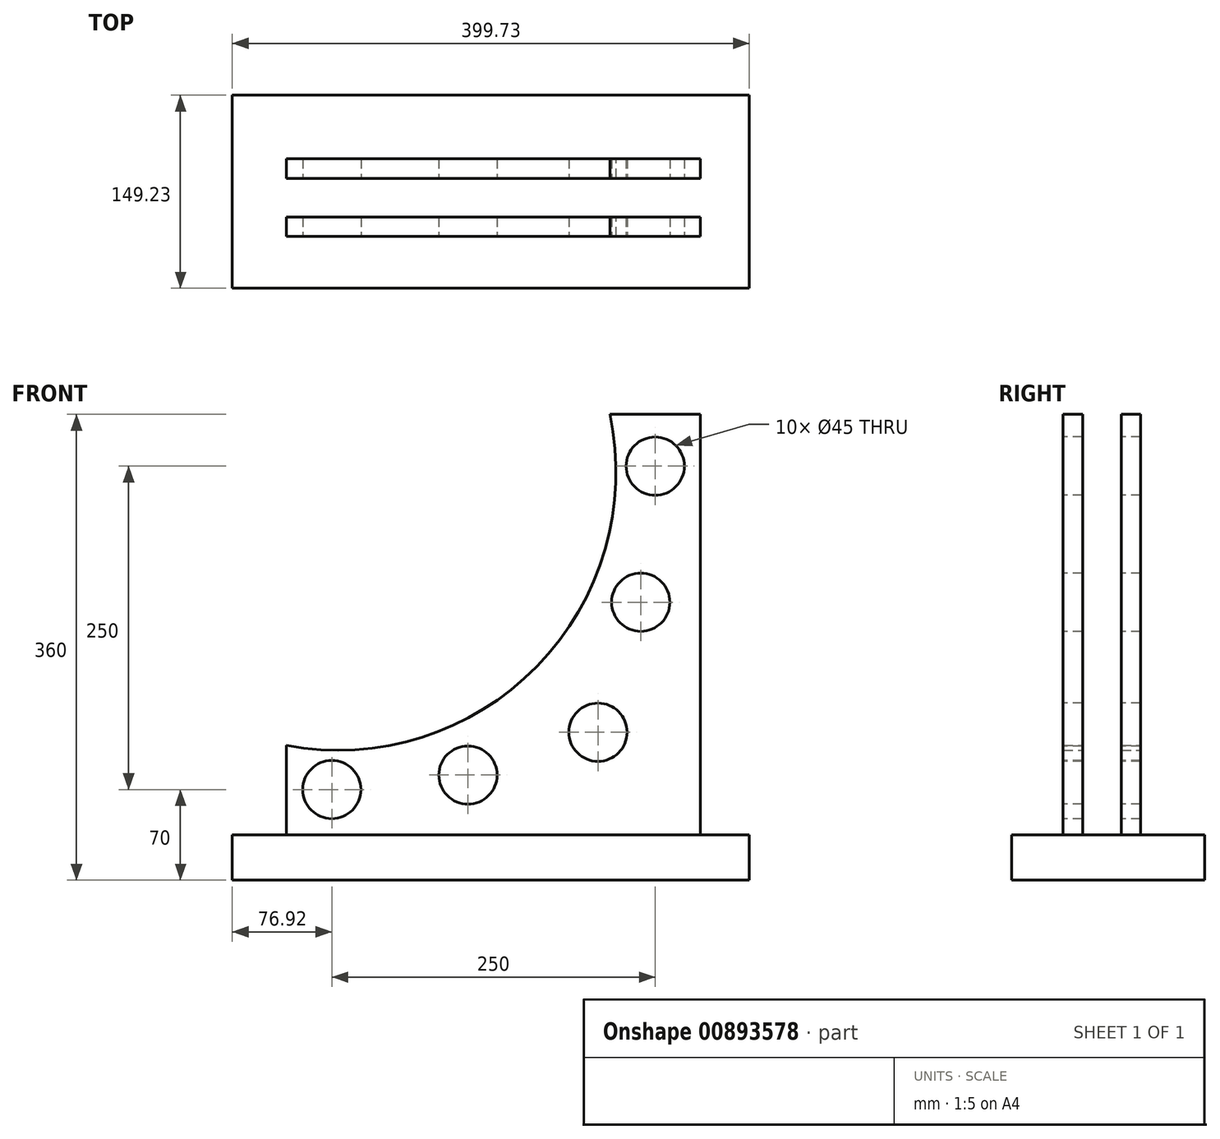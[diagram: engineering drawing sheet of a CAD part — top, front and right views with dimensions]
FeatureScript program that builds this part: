
annotation { "Feature Type Name" : "Feature", "Feature Type Description" : "" }
export const myFeature = defineFeature(function(context is Context, id is Id, definition is map)
    precondition{}
    {
        {
            var Q0;
            Q0=qCreatedBy(makeId("Top.planeOp"),FACE);
            var sketch = newSketch(context, id + "F0", { "sketchPlane" : qUnion([Q0])});
            skLineSegment(sketch, "E0.bottom", {"start": v(-320, -101.07) * mm, "end": v(0, -101.07) * mm});
            skLineSegment(sketch, "E0.top", {"start": v(-320, -41.07) * mm, "end": v(0, -41.07) * mm});
            skLineSegment(sketch, "E0.left", {"start": v(-320, -101.07) * mm, "end": v(-320, -41.07) * mm});
            skLineSegment(sketch, "E0.right", {"start": v(0, -101.07) * mm, "end": v(0, -41.07) * mm});
            skSolve(sketch);
        }
        {
            var Q0;
            Q0=makeQuery(id+"F0.imprint","IMPRINT",FACE,{"disambiguationData":[TD([[makeQuery(id+"F0.imprint","IMPRINT",EDGE,{"derivedFrom":sQuery(id+"F0.wireOp",EDGE,"E0.bottom")}),1.0]])]});
            extrude(context, id + "F1", {"entities" : qUnion([Q0]), "depth" : 360 * mm, "offsetDistance" : 25 * mm});
        }
        {
            var Q0;
            Q0=makeQuery(id+"F1.opExtrude","SWEPT_FACE",FACE,{"disambiguationData":[OSD([sQuery(id+"F0.wireOp",EDGE,"E0.bottom")])]});
            var sketch = newSketch(context, id + "F2", { "sketchPlane" : qUnion([Q0])});
            skCircle(sketch, "E1", {"center": v(-35, 320) * mm, "radius": 22.5 * mm});
            skCircle(sketch, "E2", {"center": v(-285, 70) * mm, "radius": 22.5 * mm});
            skCircle(sketch, "E3", {"center": v(-179.76, 81.2) * mm, "radius": 22.5 * mm});
            skCircle(sketch, "E4", {"center": v(-79.24, 114.3) * mm, "radius": 22.5 * mm});
            skCircle(sketch, "E5", {"center": v(-46.2, 214.76) * mm, "radius": 22.5 * mm});
            skSolve(sketch);
        }
        {
            var Q0;
            Q0=qSketchRegion(id+"F2",true);
            var Q1;
            Q1=makeQuery(id+"F1.opExtrude","SWEPT_FACE",FACE,{"disambiguationData":[OSD([sQuery(id+"F0.wireOp",EDGE,"E0.top")])]});
            extrude(context, id + "F3", {"entities" : qUnion([Q0]), "operationType" : NewBodyOperationType.REMOVE, "endBound" : BoundingType.UP_TO_SURFACE, "oppositeDirection" : true, "depth" : 25 * mm, "endBoundEntityFace" : qUnion([Q1]), "offsetDistance" : 25 * mm});
        }
        {
            var Q0;
            Q0=qCreatedBy(makeId("Front.planeOp"),FACE);
            var sketch = newSketch(context, id + "F4", { "sketchPlane" : qUnion([Q0])});
            skArc(sketch, "E6", {"start": v(-320, 104.05) * mm, "mid": v(-126.5, 165.12) * mm, "end": v(-70, 360) * mm});
            skLineSegment(sketch, "E7", {"start": v(0, 0) * mm, "end": v(-320, 360) * mm, "construction": true});
            skLineSegment(sketch, "E8", {"start": v(-320, 104.05) * mm, "end": v(-320, 360) * mm});
            skLineSegment(sketch, "E9", {"start": v(-320, 360) * mm, "end": v(-70, 360) * mm});
            skSolve(sketch);
        }
        {
            var Q0;
            Q0=qSketchRegion(id+"F4",true);
            var Q1;
            Q1=makeQuery(id+"F1.opExtrude","SWEPT_FACE",FACE,{"disambiguationData":[OSD([sQuery(id+"F0.wireOp",EDGE,"E0.bottom")])]});
            var Q2;
            Q2=makeQuery(id+"F1.opExtrude","SWEPT_FACE",FACE,{"disambiguationData":[OSD([sQuery(id+"F0.wireOp",EDGE,"E0.top")])]});
            extrude(context, id + "F5", {"entities" : qUnion([Q0]), "operationType" : NewBodyOperationType.REMOVE, "endBound" : BoundingType.UP_TO_SURFACE, "depth" : 25 * mm, "endBoundEntityFace" : qUnion([Q1]), "offsetDistance" : 25 * mm});
        }
        {
            var Q0;
            Q0=qCreatedBy(makeId("Right.planeOp"),FACE);
            var sketch = newSketch(context, id + "F6", { "sketchPlane" : qUnion([Q0])});
            skLineSegment(sketch, "E10.bottom", {"start": v(-56.07, 0) * mm, "end": v(-86.07, 0) * mm});
            skLineSegment(sketch, "E10.top", {"start": v(-56.07, 360) * mm, "end": v(-86.07, 360) * mm});
            skLineSegment(sketch, "E10.left", {"start": v(-56.07, 0) * mm, "end": v(-56.07, 360) * mm});
            skLineSegment(sketch, "E10.right", {"start": v(-86.07, 0) * mm, "end": v(-86.07, 360) * mm});
            skSolve(sketch);
        }
        {
            var Q0;
            Q0=qSketchRegion(id+"F6",true);
            var Q1;
            Q1=makeQuery(id+"F1.opExtrude","SWEPT_FACE",FACE,{"disambiguationData":[OSD([sQuery(id+"F0.wireOp",EDGE,"E0.left")])]});
            extrude(context, id + "F7", {"entities" : qUnion([Q0]), "operationType" : NewBodyOperationType.REMOVE, "endBound" : BoundingType.UP_TO_SURFACE, "oppositeDirection" : true, "depth" : 25 * mm, "endBoundEntityFace" : qUnion([Q1]), "offsetDistance" : 25 * mm});
        }
        {
            var Q0;
            {var subQ0=sQuery(id+"F0.wireOp",EDGE,"E0.bottom");var subQ1=sQuery(id+"F0.wireOp",EDGE,"E0.right");var subQ2=sQuery(id+"F0.wireOp",EDGE,"E0.left");Q0=makeQuery(id+"F7.boolean.opBoolean","SPLIT",FACE,{"disambiguationData":[TD([makeQuery(id+"F1.opExtrude","SWEPT_FACE",FACE,{"disambiguationData":[OSD([subQ0])]})])],"derivedFrom":makeQuery(id+"F1.opExtrude","CAP_FACE",FACE,{"disambiguationData":[OSD([subQ0,sQuery(id+"F0.wireOp",EDGE,"E0.top"),subQ2,subQ1])],"isStart":true})});}
            var sketch = newSketch(context, id + "F8", { "sketchPlane" : qUnion([Q0])});
            skLineSegment(sketch, "E11.bottom", {"start": v(-361.92, 141) * mm, "end": v(37.81, 141) * mm});
            skLineSegment(sketch, "E11.top", {"start": v(-361.92, -8.22) * mm, "end": v(37.81, -8.22) * mm});
            skLineSegment(sketch, "E11.left", {"start": v(-361.92, 141) * mm, "end": v(-361.92, -8.22) * mm});
            skLineSegment(sketch, "E11.right", {"start": v(37.81, 141) * mm, "end": v(37.81, -8.22) * mm});
            skSolve(sketch);
        }
        {
            var Q0;
            Q0=makeQuery(id+"F8.imprint","IMPRINT",FACE,{"disambiguationData":[TD([[makeQuery(id+"F8.imprint","IMPRINT",EDGE,{"derivedFrom":sQuery(id+"F8.wireOp",EDGE,"E11.bottom")}),-1.0]])]});
            extrude(context, id + "F9", {"entities" : qUnion([Q0]), "operationType" : NewBodyOperationType.ADD, "oppositeDirection" : true, "depth" : 35 * mm, "offsetDistance" : 25 * mm});
        }
    });
